# Revit family: Haworth_Accessory_MonitorArm_HeavyDuty
name_source: partatom
category: Furniture Systems
revit_build: Autodesk Revit 2018 (Build: 20170223_1515(x64)
units: mm (PartAtom-declared; Revit-internal decimal feet)

## family parameters
Always vertical = Yes
Cut with Voids When Loaded = No
OmniClass Number = 23.40.70.14.64.21
OmniClass Title = Systems Furniture
Part Type = Normal
Room Calculation Point = No
Round Connector Dimension = Use Diameter
Shared = No
Work Plane-Based = No

## types (2) — shared parameters
Actual Depth = 1 1/4"
Assembly Code = E2020200
Base of Arm = 3 3/8"
Description = Haworth - Accessory - Monitor Arm - Heavy Duty
Double Arm = Yes
Manufacturer = Haworth
Model = Haworth - Accessory - Monitor Arm - Heavy Duty
Post Base = 3 1/2"
Revision Number = 3
Single = No
Single Monitor Location = 2 1/4"
Size = Verify Final Dim. w/ Haworth
Spacer = 1 3/32"
Sustainability Info = http://www.haworth.com
Tool Rail = 4 3/8"
Tool Rail Mounting Height = 7 7/16"
Trim Finish = Haworth _ Paint _ Metallic Champagne
URL = www.haworth.com
URL - Product = http://www.haworth.com
Warranty = http://www.haworth.com

## type names (no varying parameters)
- Single Monitor Arm
- Double Monitor Arm

## geometry (parser evidence)
native form markers: Sweep x12
no freeform markers — native parametric forms only
